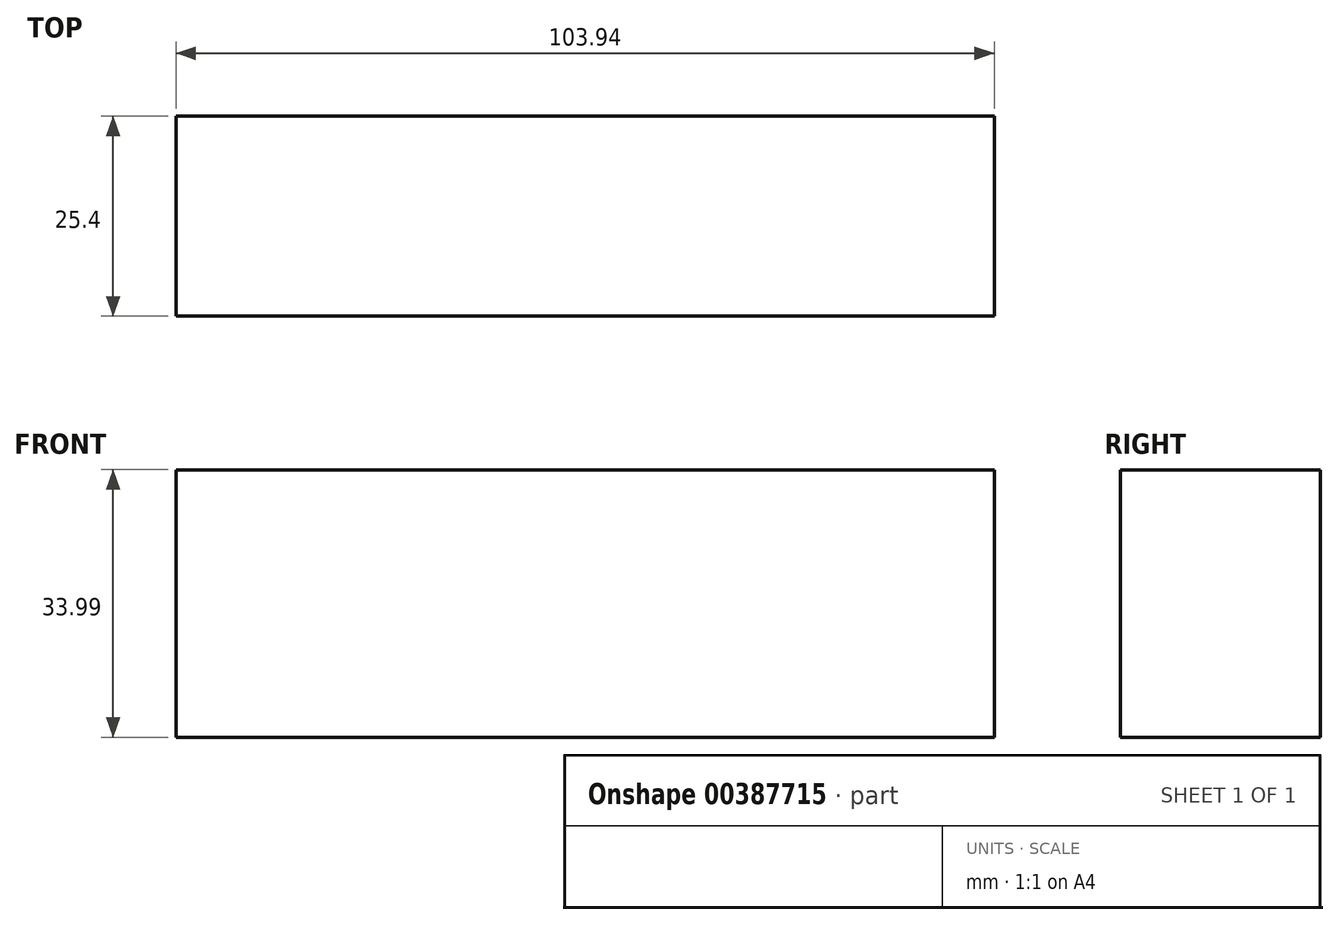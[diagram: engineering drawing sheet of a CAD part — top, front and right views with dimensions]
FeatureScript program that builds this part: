
annotation { "Feature Type Name" : "Feature", "Feature Type Description" : "" }
export const myFeature = defineFeature(function(context is Context, id is Id, definition is map)
    precondition{}
    {
        {
            var Q0;
            Q0=qCreatedBy(makeId("Front.planeOp"),FACE);
            var sketch = newSketch(context, id + "F0", { "sketchPlane" : qUnion([Q0])});
            skLineSegment(sketch, "E0.bottom", {"start": v(0, 0) * mm, "end": v(103.94, 0) * mm});
            skLineSegment(sketch, "E0.top", {"start": v(0, 33.99) * mm, "end": v(103.94, 33.99) * mm});
            skLineSegment(sketch, "E0.left", {"start": v(0, 0) * mm, "end": v(0, 33.99) * mm});
            skLineSegment(sketch, "E0.right", {"start": v(103.94, 0) * mm, "end": v(103.94, 33.99) * mm});
            skSolve(sketch);
        }
        {
            var Q0;
            Q0 = qSketchRegion(id + "F0", true);
            extrude(context, id + "F1", {"entities" : qUnion([Q0]), "depth" : 25.4 * mm});
        }
    });
